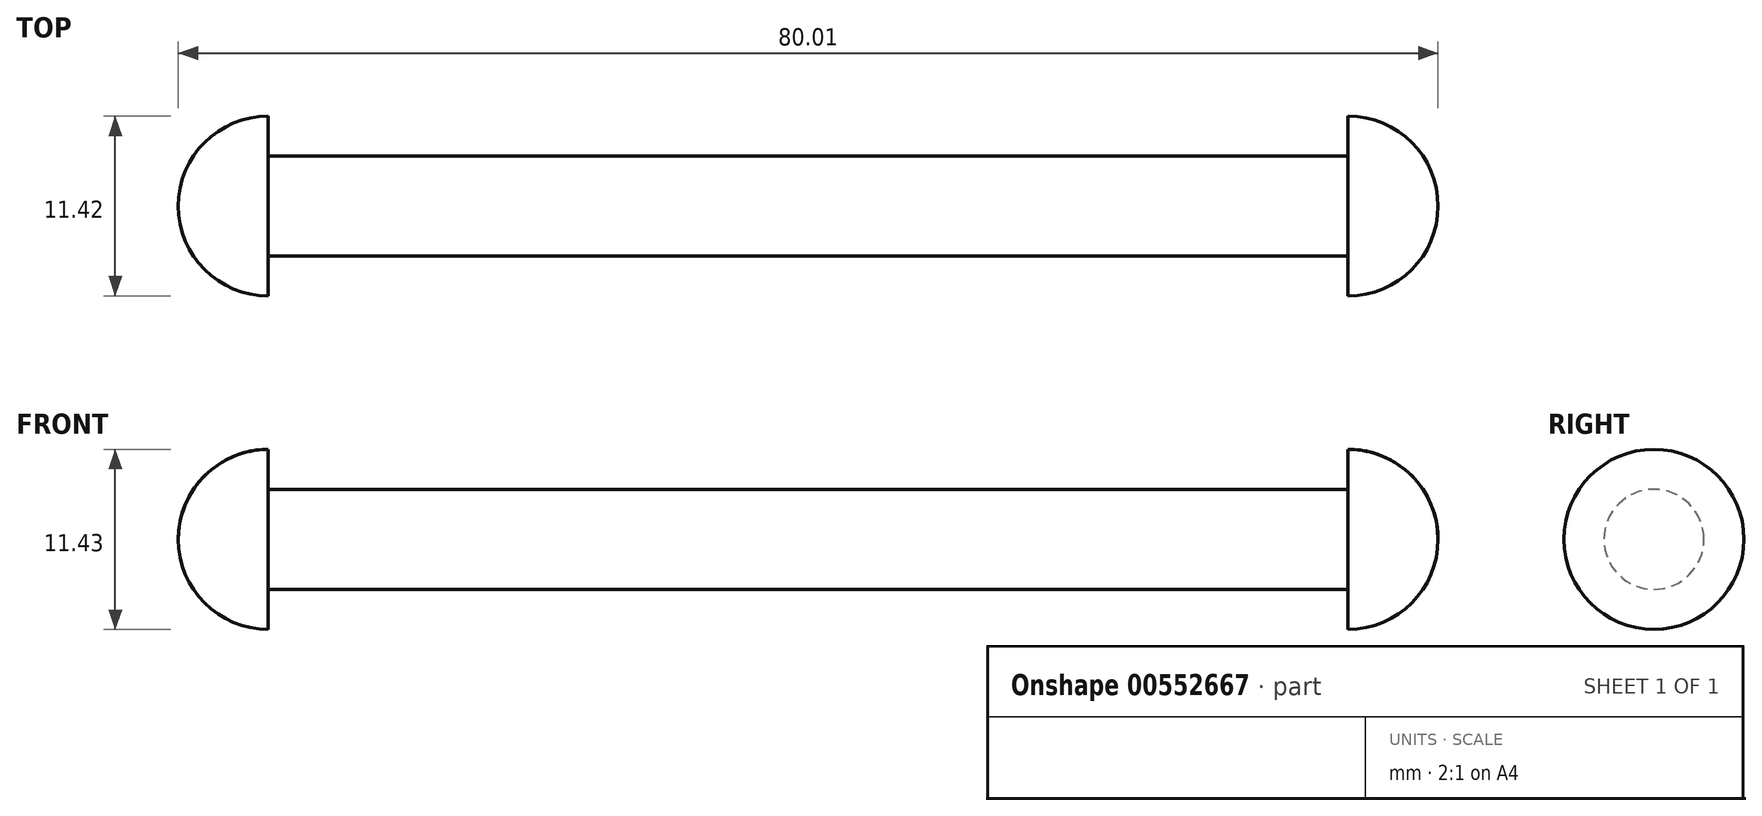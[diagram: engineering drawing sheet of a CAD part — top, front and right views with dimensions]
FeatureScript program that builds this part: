
annotation { "Feature Type Name" : "Feature", "Feature Type Description" : "" }
export const myFeature = defineFeature(function(context is Context, id is Id, definition is map)
    precondition{}
    {
        {
            var Q0;
            Q0=qCreatedBy(makeId("Front.planeOp"),FACE);
            var sketch = newSketch(context, id + "F0", { "sketchPlane" : qUnion([Q0])});
            skLineSegment(sketch, "E0", {"start": v(-46.65, 9.9) * mm, "end": v(21.93, 9.9) * mm});
            skArc(sketch, "E1", {"start": v(27.65, 9.9) * mm, "mid": v(25.97, 13.95) * mm, "end": v(21.93, 15.62) * mm});
            skLineSegment(sketch, "E2.0", {"start": v(-46.65, 13.08) * mm, "end": v(21.93, 13.08) * mm});
            skLineSegment(sketch, "E3", {"start": v(-46.65, 13.08) * mm, "end": v(-46.65, 15.62) * mm});
            skLineSegment(sketch, "E4", {"start": v(21.93, 13.08) * mm, "end": v(21.93, 15.62) * mm});
            skLineSegment(sketch, "E5", {"start": v(21.93, 15.62) * mm, "end": v(21.93, 13.08) * mm});
            skLineSegment(sketch, "E6", {"start": v(-52.36, 9.9) * mm, "end": v(27.65, 9.9) * mm});
            skPoint(sketch, "E7.orphan", {"position": v(-56.77, 9.9) * mm});
            skArc(sketch, "E8.trimOffspring", {"start": v(-46.65, 15.62) * mm, "mid": v(-50.69, 13.95) * mm, "end": v(-52.36, 9.9) * mm});
            skSolve(sketch);
        }
        {
            var Q0;
            Q0 = qSketchRegion(id + "F0", true);
            var Q1;
            Q1=sQuery(id+"F0.wireOp",EDGE,"E6");
            revolve(context, id + "F1", {"entities" : qUnion([Q0]), "axis" : qUnion([Q1]), "revolveType" : RevolveType.FULL});
        }
    });
